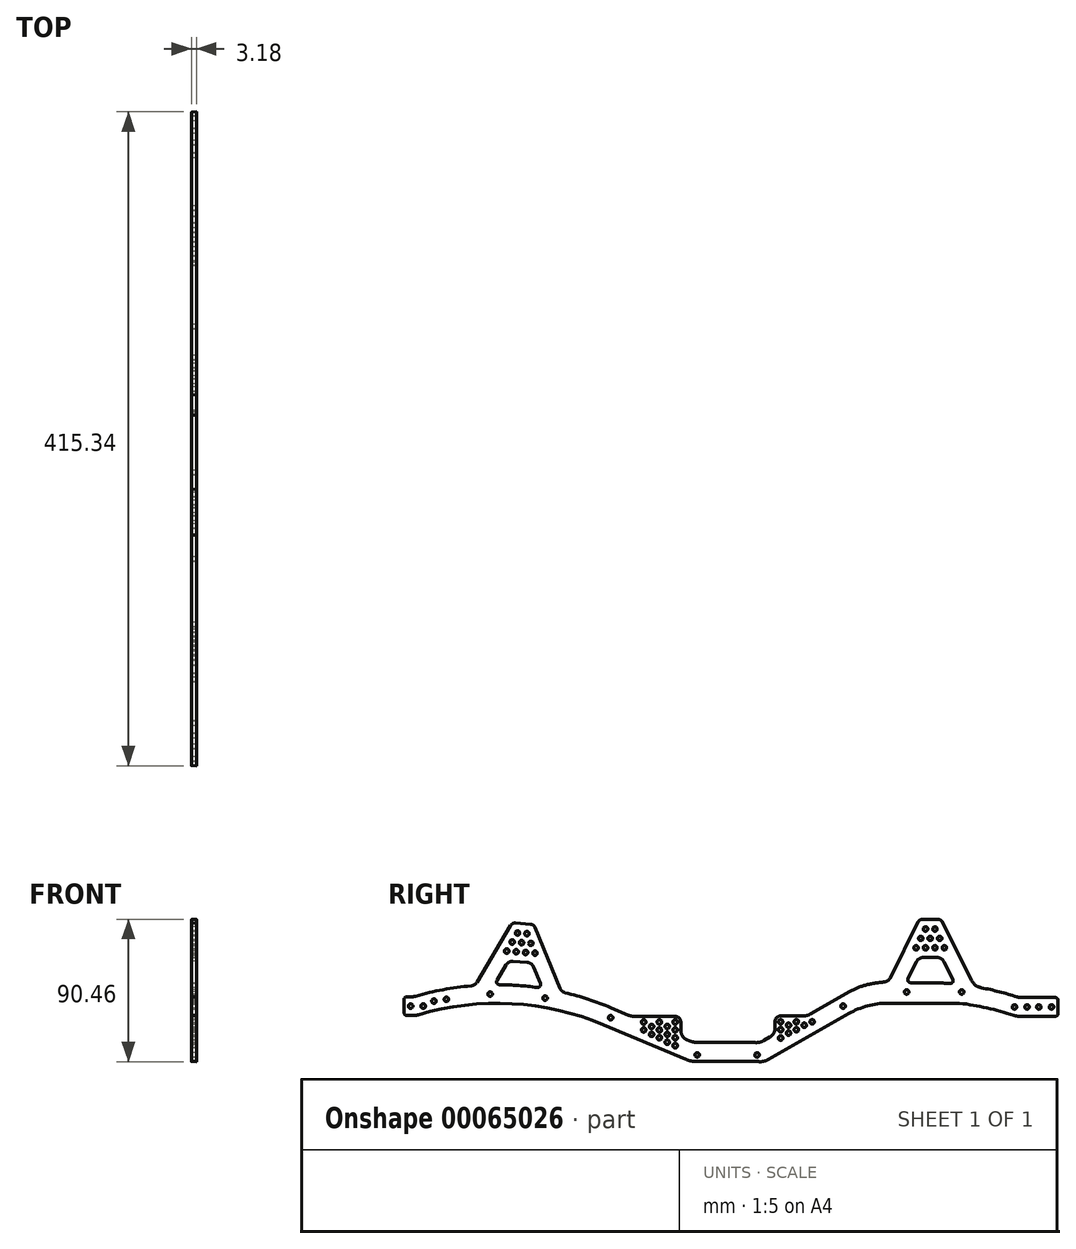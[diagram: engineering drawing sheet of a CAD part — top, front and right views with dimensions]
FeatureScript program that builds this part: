
annotation { "Feature Type Name" : "Feature", "Feature Type Description" : "" }
export const myFeature = defineFeature(function(context is Context, id is Id, definition is map)
    precondition{}
    {
        {
            var Q0;
            Q0=qCreatedBy(makeId("Right.planeOp"),FACE);
            var sketch = newSketch(context, id + "F0", { "sketchPlane" : qUnion([Q0])});
            skLineSegment(sketch, "E0.bottom", {"start": v(-1.5, 0) * mm, "end": v(-24.72, 0) * mm});
            skLineSegment(sketch, "E0.top", {"start": v(-1.5, 11.5) * mm, "end": v(-22.88, 11.5) * mm});
            skLineSegment(sketch, "E0.left", {"start": v(0, 1.5) * mm, "end": v(0, 10) * mm});
            skCircle(sketch, "E1", {"center": v(-4, 5.75) * mm, "radius": 1.59 * mm});
            skPoint(sketch, "E1.centerSnap0", {"position": v(0, 5.75) * mm});
            skCircle(sketch, "E2", {"center": v(-12, 5.75) * mm, "radius": 1.59 * mm});
            skCircle(sketch, "E3", {"center": v(-19.5, 5.75) * mm, "radius": 1.59 * mm});
            skCircle(sketch, "E4", {"center": v(-27.5, 5.75) * mm, "radius": 1.59 * mm});
            skCircle(sketch, "E5", {"center": v(-61, 15.25) * mm, "radius": 1.59 * mm});
            skCircle(sketch, "E6", {"center": v(-96, 15.25) * mm, "radius": 1.59 * mm});
            skLineSegment(sketch, "E7.top", {"start": v(-107.96, 8.28) * mm, "end": v(-62.46, 8.28) * mm});
            skCircle(sketch, "E8", {"center": v(-90, 43.28) * mm, "radius": 1.59 * mm});
            skCircle(sketch, "E9", {"center": v(-84, 43.28) * mm, "radius": 1.59 * mm});
            skCircle(sketch, "E10", {"center": v(-78, 43.28) * mm, "radius": 1.59 * mm});
            skCircle(sketch, "E11", {"center": v(-72, 43.28) * mm, "radius": 1.59 * mm});
            skCircle(sketch, "E12", {"center": v(-87, 49.28) * mm, "radius": 1.59 * mm});
            skCircle(sketch, "E13", {"center": v(-81, 49.28) * mm, "radius": 1.59 * mm});
            skCircle(sketch, "E14", {"center": v(-75, 49.28) * mm, "radius": 1.59 * mm});
            skCircle(sketch, "E15", {"center": v(-84, 55.28) * mm, "radius": 1.59 * mm});
            skCircle(sketch, "E16", {"center": v(-78, 55.28) * mm, "radius": 1.59 * mm});
            skLineSegment(sketch, "E17", {"start": v(-90, 37.39) * mm, "end": v(-90, 67.96) * mm, "construction": true});
            skLineSegment(sketch, "E18", {"start": v(-103.26, 43.28) * mm, "end": v(-65.64, 43.28) * mm, "construction": true});
            skLineSegment(sketch, "E19", {"start": v(-106.28, 24.14) * mm, "end": v(-88.54, 59.62) * mm});
            skLineSegment(sketch, "E20", {"start": v(-85.85, 61.28) * mm, "end": v(-76.15, 61.28) * mm});
            skLineSegment(sketch, "E21", {"start": v(-73.46, 59.62) * mm, "end": v(-54.94, 22.59) * mm});
            skLineSegment(sketch, "E22", {"start": v(-95.22, 23.9) * mm, "end": v(-89.9, 34.52) * mm});
            skLineSegment(sketch, "E23", {"start": v(-85.44, 37.28) * mm, "end": v(-76.56, 37.28) * mm});
            skLineSegment(sketch, "E24", {"start": v(-72.1, 34.52) * mm, "end": v(-66.49, 23.31) * mm});
            skLineSegment(sketch, "E25.trimOffspring", {"start": v(-93.43, 21) * mm, "end": v(-83, 21) * mm});
            skCircle(sketch, "E26", {"center": v(-166, -8.72) * mm, "radius": 1.59 * mm});
            skCircle(sketch, "E27", {"center": v(-166, -3.72) * mm, "radius": 1.59 * mm});
            skCircle(sketch, "E28", {"center": v(-161, -5.86) * mm, "radius": 1.59 * mm});
            skCircle(sketch, "E29", {"center": v(-191, -24.72) * mm, "radius": 1.59 * mm});
            skLineSegment(sketch, "E30", {"start": v(-183.93, -27.53) * mm, "end": v(-132.76, 1.7) * mm});
            skLineSegment(sketch, "E31", {"start": v(-186.53, -15.77) * mm, "end": v(-182.64, -13.55) * mm});
            skLineSegment(sketch, "E32.trimOffspring", {"start": v(-156.92, 1.14) * mm, "end": v(-131.8, 15.49) * mm});
            skLineSegment(sketch, "E33.bottom", {"start": v(-228.31, -17.04) * mm, "end": v(-192.48, -17.04) * mm});
            skCircle(sketch, "E34", {"center": v(-229, -24.72) * mm, "radius": 1.59 * mm});
            skLineSegment(sketch, "E35.trimOffspring", {"start": v(-415.34, -41.7) * mm, "end": v(-30.28, -41.7) * mm, "construction": true});
            skCircle(sketch, "E36", {"center": v(-253, -8.85) * mm, "radius": 1.59 * mm});
            skArc(sketch, "E37", {"start": v(-27.9, 0.52) * mm, "mid": v(-44.98, 5.28) * mm, "end": v(-62.46, 8.28) * mm});
            skArc(sketch, "E38.trimOffspring", {"start": v(-25.96, 11.99) * mm, "mid": v(-37.17, 15.23) * mm, "end": v(-48.57, 17.77) * mm});
            skArc(sketch, "E39.trimOffspring", {"start": v(-68.44, 20.43) * mm, "mid": v(-75.71, 20.86) * mm, "end": v(-83, 21) * mm});
            skArc(sketch, "E40.filletArc", {"start": v(-107.96, 8.28) * mm, "mid": v(-120.79, 6.6) * mm, "end": v(-132.76, 1.7) * mm});
            skPoint(sketch, "E41.visualSharp", {"position": v(-73.47, 37.28) * mm});
            skArc(sketch, "E41.filletArc", {"start": v(-72.1, 34.52) * mm, "mid": v(-73.93, 36.53) * mm, "end": v(-76.56, 37.28) * mm});
            skPoint(sketch, "E42.visualSharp", {"position": v(-88.53, 37.28) * mm});
            skArc(sketch, "E42.filletArc", {"start": v(-85.44, 37.28) * mm, "mid": v(-88.07, 36.53) * mm, "end": v(-89.9, 34.52) * mm});
            skPoint(sketch, "E43.visualSharp", {"position": v(-96.67, 21) * mm});
            skArc(sketch, "E43.filletArc", {"start": v(-95.22, 23.9) * mm, "mid": v(-95.13, 21.95) * mm, "end": v(-93.43, 21) * mm});
            skPoint(sketch, "E44.visualSharp", {"position": v(-64.89, 20.11) * mm});
            skArc(sketch, "E44.filletArc", {"start": v(-68.44, 20.43) * mm, "mid": v(-66.62, 21.3) * mm, "end": v(-66.49, 23.31) * mm});
            skPoint(sketch, "E45.visualSharp", {"position": v(-87.7, 61.28) * mm});
            skArc(sketch, "E45.filletArc", {"start": v(-85.85, 61.28) * mm, "mid": v(-87.43, 60.83) * mm, "end": v(-88.54, 59.62) * mm});
            skPoint(sketch, "E46.visualSharp", {"position": v(-74.3, 61.28) * mm});
            skArc(sketch, "E46.filletArc", {"start": v(-73.46, 59.62) * mm, "mid": v(-74.57, 60.83) * mm, "end": v(-76.15, 61.28) * mm});
            skPoint(sketch, "E47.visualSharp", {"position": v(-52.92, 18.54) * mm});
            skArc(sketch, "E47.filletArc", {"start": v(-54.94, 22.59) * mm, "mid": v(-52.32, 19.43) * mm, "end": v(-48.57, 17.77) * mm});
            skPoint(sketch, "E48.visualSharp", {"position": v(-24.48, 11.5) * mm});
            skArc(sketch, "E48.filletArc", {"start": v(-25.96, 11.99) * mm, "mid": v(-24.44, 11.62) * mm, "end": v(-22.88, 11.5) * mm});
            skPoint(sketch, "E49.visualSharp", {"position": v(-26.38, 0) * mm});
            skArc(sketch, "E49.filletArc", {"start": v(-27.9, 0.52) * mm, "mid": v(-26.33, 0.13) * mm, "end": v(-24.72, 0) * mm});
            skPoint(sketch, "E50.visualSharp", {"position": v(0, 11.5) * mm});
            skArc(sketch, "E50.filletArc", {"start": v(0, 10) * mm, "mid": v(-0.44, 11.06) * mm, "end": v(-1.5, 11.5) * mm});
            skPoint(sketch, "E51.visualSharp", {"position": v(0, 0) * mm});
            skArc(sketch, "E51.filletArc", {"start": v(-1.5, 0) * mm, "mid": v(-0.44, 0.44) * mm, "end": v(0, 1.5) * mm});
            skPoint(sketch, "E52.visualSharp", {"position": v(-169.55, -6.07) * mm});
            skArc(sketch, "E53.filletArc", {"start": v(-192.48, -17.04) * mm, "mid": v(-189.4, -16.87) * mm, "end": v(-186.53, -15.77) * mm});
            skPoint(sketch, "E54.visualSharp", {"position": v(-187.05, -29.31) * mm});
            skArc(sketch, "E54.filletArc", {"start": v(-190.42, -28.72) * mm, "mid": v(-187.07, -28.68) * mm, "end": v(-183.93, -27.53) * mm});
            skLineSegment(sketch, "E55", {"start": v(-107.44, 25.98) * mm, "end": v(-107.44, 25.98) * mm});
            skLineSegment(sketch, "E56", {"start": v(-190.42, -28.72) * mm, "end": v(-230.42, -28.65) * mm});
            skCircle(sketch, "E57", {"center": v(-253, -13.85) * mm, "radius": 1.59 * mm});
            skCircle(sketch, "E58", {"center": v(-253, -3.85) * mm, "radius": 1.59 * mm});
            skCircle(sketch, "E59", {"center": v(-258, -6.68) * mm, "radius": 1.59 * mm});
            skCircle(sketch, "E60", {"center": v(-411, 6.28) * mm, "radius": 1.59 * mm});
            skLineSegment(sketch, "E61", {"start": v(-411, 6.28) * mm, "end": v(-205.2, 8.89) * mm, "construction": true});
            skCircle(sketch, "E62", {"center": v(-403, 6.28) * mm, "radius": 1.59 * mm});
            skLineSegment(sketch, "E63", {"start": v(-415, 2.03) * mm, "end": v(-415, 10.53) * mm});
            skCircle(sketch, "E64", {"center": v(-360.5, 13.92) * mm, "radius": 1.59 * mm});
            skCircle(sketch, "E65", {"center": v(-325.6, 11.36) * mm, "radius": 1.59 * mm});
            skCircle(sketch, "E66", {"center": v(-396.21, 9.47) * mm, "radius": 1.59 * mm});
            skCircle(sketch, "E67", {"center": v(-388.29, 10.57) * mm, "radius": 1.59 * mm});
            skCircle(sketch, "E68", {"center": v(-284, -1.11) * mm, "radius": 1.59 * mm});
            skArc(sketch, "E69", {"start": v(-288.38, -5.48) * mm, "mid": v(-346.64, 7.96) * mm, "end": v(-406.02, 0.95) * mm});
            skArc(sketch, "E70", {"start": v(-283.9, 5.12) * mm, "mid": v(-298.2, 10.46) * mm, "end": v(-312.88, 14.62) * mm});
            skLineSegment(sketch, "E71", {"start": v(-413.5, 12.03) * mm, "end": v(-410.53, 12.03) * mm});
            skLineSegment(sketch, "E72", {"start": v(-413.5, 0.53) * mm, "end": v(-408.88, 0.53) * mm});
            skLineSegment(sketch, "E73", {"start": v(-236.22, -27.47) * mm, "end": v(-288.38, -5.48) * mm});
            skLineSegment(sketch, "E74", {"start": v(-234.14, -15.86) * mm, "end": v(-235.68, -15.21) * mm});
            skPoint(sketch, "E75.visualSharp", {"position": v(-169.43, -0.18) * mm});
            skPoint(sketch, "E76.visualSharp", {"position": v(-159.22, -0.18) * mm});
            skArc(sketch, "E76.filletArc", {"start": v(-161.88, -0.18) * mm, "mid": v(-159.31, 0.16) * mm, "end": v(-156.92, 1.14) * mm});
            skLineSegment(sketch, "E77", {"start": v(-360.5, 13.92) * mm, "end": v(-325.6, 11.36) * mm, "construction": true});
            skLineSegment(sketch, "E78", {"start": v(-322.64, 51.7) * mm, "end": v(-325.6, 11.36) * mm, "construction": true});
            skLineSegment(sketch, "E79", {"start": v(-357.62, 53.24) * mm, "end": v(-360.5, 13.92) * mm, "construction": true});
            skCircle(sketch, "E80", {"center": v(-340.56, 46.55) * mm, "radius": 1.59 * mm});
            skLineSegment(sketch, "E81", {"start": v(-358.02, 47.83) * mm, "end": v(-323.1, 45.27) * mm, "construction": true});
            skCircle(sketch, "E82", {"center": v(-334.58, 46.11) * mm, "radius": 1.59 * mm});
            skCircle(sketch, "E83", {"center": v(-346.55, 46.99) * mm, "radius": 1.59 * mm});
            skCircle(sketch, "E84", {"center": v(-349.98, 41.22) * mm, "radius": 1.59 * mm});
            skCircle(sketch, "E85", {"center": v(-344, 40.79) * mm, "radius": 1.59 * mm});
            skCircle(sketch, "E86", {"center": v(-338, 40.35) * mm, "radius": 1.59 * mm});
            skCircle(sketch, "E87", {"center": v(-332.02, 39.9) * mm, "radius": 1.59 * mm});
            skCircle(sketch, "E88", {"center": v(-343.12, 52.75) * mm, "radius": 1.59 * mm});
            skCircle(sketch, "E89", {"center": v(-337.13, 52.31) * mm, "radius": 1.59 * mm});
            skLineSegment(sketch, "E90", {"start": v(-357.58, 53.81) * mm, "end": v(-322.67, 51.25) * mm, "construction": true});
            skLineSegment(sketch, "E91", {"start": v(-358.45, 41.84) * mm, "end": v(-323.55, 39.29) * mm, "construction": true});
            skLineSegment(sketch, "E92", {"start": v(-339.67, 58.73) * mm, "end": v(-341.5, 33.86) * mm, "construction": true});
            skLineSegment(sketch, "E93", {"start": v(-347.32, 57.41) * mm, "end": v(-368.74, 21.42) * mm});
            skLineSegment(sketch, "E94", {"start": v(-344.53, 58.87) * mm, "end": v(-334.84, 58.16) * mm});
            skLineSegment(sketch, "E95", {"start": v(-332.29, 56.31) * mm, "end": v(-316.34, 17.58) * mm});
            skLineSegment(sketch, "E96", {"start": v(-356.32, 22.74) * mm, "end": v(-350.53, 32.48) * mm});
            skLineSegment(sketch, "E97", {"start": v(-345.86, 34.9) * mm, "end": v(-337.01, 34.26) * mm});
            skLineSegment(sketch, "E98", {"start": v(-332.75, 31.17) * mm, "end": v(-328.44, 20.7) * mm});
            skCircle(sketch, "E99", {"center": v(-263, -3.85) * mm, "radius": 1.59 * mm});
            skCircle(sketch, "E100", {"center": v(-263, -8.85) * mm, "radius": 1.59 * mm});
            skEllipticalArc(sketch, "E101.trimOffspring", {});
            skPoint(sketch, "E102.visualSharp", {"position": v(-127.63, 17.87) * mm});
            skArc(sketch, "E102.filletArc", {"start": v(-120.81, 19.76) * mm, "mid": v(-126.46, 18.03) * mm, "end": v(-131.8, 15.49) * mm});
            skPoint(sketch, "E103.visualSharp", {"position": v(-107.55, 21.59) * mm});
            skArc(sketch, "E103.filletArc", {"start": v(-110.32, 21.4) * mm, "mid": v(-107.94, 22.24) * mm, "end": v(-106.28, 24.14) * mm});
            skCircle(sketch, "E104", {"center": v(-136.33, 6.28) * mm, "radius": 1.59 * mm});
            skPoint(sketch, "E105.visualSharp", {"position": v(-233.44, -28.64) * mm});
            skArc(sketch, "E105.filletArc", {"start": v(-236.22, -27.47) * mm, "mid": v(-233.38, -28.35) * mm, "end": v(-230.42, -28.65) * mm});
            skPoint(sketch, "E106.visualSharp", {"position": v(-231.34, -17.04) * mm});
            skArc(sketch, "E106.filletArc", {"start": v(-234.14, -15.86) * mm, "mid": v(-231.28, -16.74) * mm, "end": v(-228.31, -17.04) * mm});
            skPoint(sketch, "E107.visualSharp", {"position": v(-249.54, -0.18) * mm});
            skPoint(sketch, "E108.newPointB", {"position": v(-284, 5.15) * mm});
            skLineSegment(sketch, "E109", {"start": v(-284, 5.15) * mm, "end": v(-272.64, 0.37) * mm});
            skPoint(sketch, "E110.visualSharp", {"position": v(-270.72, -0.44) * mm});
            skArc(sketch, "E110.filletArc", {"start": v(-272.64, 0.37) * mm, "mid": v(-270.68, -0.23) * mm, "end": v(-268.63, -0.42) * mm});
            skPoint(sketch, "E111.visualSharp", {"position": v(-348.95, 35.13) * mm});
            skArc(sketch, "E111.filletArc", {"start": v(-345.86, 34.9) * mm, "mid": v(-348.54, 34.35) * mm, "end": v(-350.53, 32.48) * mm});
            skPoint(sketch, "E112.visualSharp", {"position": v(-333.93, 34.03) * mm});
            skArc(sketch, "E112.filletArc", {"start": v(-332.75, 31.17) * mm, "mid": v(-334.45, 33.32) * mm, "end": v(-337.01, 34.26) * mm});
            skArc(sketch, "E113.trimOffspring", {"start": v(-330.57, 17.95) * mm, "mid": v(-342.56, 19.22) * mm, "end": v(-354.62, 19.72) * mm});
            skArc(sketch, "E114.trimOffspring", {"start": v(-372.6, 19) * mm, "mid": v(-390.34, 16.55) * mm, "end": v(-407.76, 12.42) * mm});
            skPoint(sketch, "E115.visualSharp", {"position": v(-358.12, 19.71) * mm});
            skArc(sketch, "E115.filletArc", {"start": v(-356.32, 22.74) * mm, "mid": v(-356.35, 20.73) * mm, "end": v(-354.62, 19.72) * mm});
            skPoint(sketch, "E116.visualSharp", {"position": v(-327.1, 17.44) * mm});
            skArc(sketch, "E116.filletArc", {"start": v(-330.57, 17.95) * mm, "mid": v(-328.7, 18.7) * mm, "end": v(-328.44, 20.7) * mm});
            skPoint(sketch, "E117.visualSharp", {"position": v(-370.06, 19.2) * mm});
            skArc(sketch, "E117.filletArc", {"start": v(-372.6, 19) * mm, "mid": v(-370.38, 19.74) * mm, "end": v(-368.74, 21.42) * mm});
            skPoint(sketch, "E118.visualSharp", {"position": v(-315.36, 15.2) * mm});
            skArc(sketch, "E118.filletArc", {"start": v(-316.34, 17.58) * mm, "mid": v(-314.97, 15.68) * mm, "end": v(-312.88, 14.62) * mm});
            skPoint(sketch, "E119.visualSharp", {"position": v(-333, 58.03) * mm});
            skArc(sketch, "E119.filletArc", {"start": v(-332.29, 56.31) * mm, "mid": v(-333.3, 57.6) * mm, "end": v(-334.84, 58.16) * mm});
            skPoint(sketch, "E120.visualSharp", {"position": v(-346.38, 59) * mm});
            skArc(sketch, "E120.filletArc", {"start": v(-344.53, 58.87) * mm, "mid": v(-346.13, 58.54) * mm, "end": v(-347.32, 57.41) * mm});
            skPoint(sketch, "E121.visualSharp", {"position": v(-415, 12.03) * mm});
            skArc(sketch, "E121.filletArc", {"start": v(-413.5, 12.03) * mm, "mid": v(-414.56, 11.6) * mm, "end": v(-415, 10.53) * mm});
            skPoint(sketch, "E122.visualSharp", {"position": v(-415, 0.53) * mm});
            skArc(sketch, "E122.filletArc", {"start": v(-415, 2.03) * mm, "mid": v(-414.56, 0.97) * mm, "end": v(-413.5, 0.53) * mm});
            skPoint(sketch, "E123.visualSharp", {"position": v(-409.1, 12.03) * mm});
            skArc(sketch, "E123.filletArc", {"start": v(-410.53, 12.03) * mm, "mid": v(-409.13, 12.13) * mm, "end": v(-407.76, 12.42) * mm});
            skPoint(sketch, "E124.visualSharp", {"position": v(-407.4, 0.53) * mm});
            skArc(sketch, "E124.filletArc", {"start": v(-408.88, 0.53) * mm, "mid": v(-407.43, 0.63) * mm, "end": v(-406.02, 0.95) * mm});
            skPoint(sketch, "E125.visualSharp", {"position": v(-244.23, -0.42) * mm});
            skPoint(sketch, "E126.visualSharp", {"position": v(-244.23, -11.61) * mm});
            skPoint(sketch, "E52.filletArc.end.orphan", {"position": v(-169.53, -5.18) * mm});
            skPoint(sketch, "E127.center.orphan", {"position": v(-258, -11.68) * mm});
            skCircle(sketch, "E128", {"center": v(-258, -11.68) * mm, "radius": 1.59 * mm});
            skPoint(sketch, "E129.center.orphan", {"position": v(-248, -13.85) * mm});
            skPoint(sketch, "E130.center.orphan", {"position": v(-248, -8.85) * mm});
            skPoint(sketch, "E125.filletArc.center.orphan", {"position": v(-248, -3.85) * mm});
            skCircle(sketch, "E131", {"center": v(-248, -16.68) * mm, "radius": 1.59 * mm});
            skCircle(sketch, "E132", {"center": v(-248, -11.68) * mm, "radius": 1.59 * mm});
            skCircle(sketch, "E133", {"center": v(-248, -6.68) * mm, "radius": 1.59 * mm});
            skCircle(sketch, "E134", {"center": v(-243, -8.85) * mm, "radius": 1.59 * mm});
            skCircle(sketch, "E135", {"center": v(-243, -3.85) * mm, "radius": 1.59 * mm});
            skCircle(sketch, "E136", {"center": v(-243, -13.85) * mm, "radius": 1.59 * mm});
            skCircle(sketch, "E137", {"center": v(-243, -18.85) * mm, "radius": 1.59 * mm});
            skLineSegment(sketch, "E138", {"start": v(-268.63, -0.42) * mm, "end": v(-243, -0.42) * mm});
            skLineSegment(sketch, "E139", {"start": v(-239.56, -3.85) * mm, "end": v(-239.56, -9.36) * mm});
            skPoint(sketch, "E140.visualSharp", {"position": v(-239.56, -13.58) * mm});
            skArc(sketch, "E140.filletArc", {"start": v(-239.56, -9.36) * mm, "mid": v(-238.5, -12.87) * mm, "end": v(-235.68, -15.21) * mm});
            skPoint(sketch, "E141.visualSharp", {"position": v(-239.56, -0.42) * mm});
            skArc(sketch, "E141.filletArc", {"start": v(-239.56, -3.85) * mm, "mid": v(-240.57, -1.42) * mm, "end": v(-243, -0.42) * mm});
            skPoint(sketch, "E142.center.orphan", {"position": v(-156, -3.72) * mm});
            skPoint(sketch, "E143.center.orphan", {"position": v(-156, -8.7) * mm});
            skCircle(sketch, "E144", {"center": v(-156, -3.72) * mm, "radius": 1.59 * mm});
            skCircle(sketch, "E145", {"center": v(-171, -10.86) * mm, "radius": 1.59 * mm});
            skCircle(sketch, "E146", {"center": v(-171, -5.86) * mm, "radius": 1.59 * mm});
            skCircle(sketch, "E147", {"center": v(-176, -3.72) * mm, "radius": 1.59 * mm});
            skCircle(sketch, "E148", {"center": v(-176, -8.7) * mm, "radius": 1.59 * mm});
            skCircle(sketch, "E149", {"center": v(-176, -14.02) * mm, "radius": 1.59 * mm});
            skLineSegment(sketch, "E150", {"start": v(-179.44, -8.04) * mm, "end": v(-179.44, -3.6) * mm});
            skLineSegment(sketch, "E151", {"start": v(-161.88, -0.18) * mm, "end": v(-176, -0.18) * mm});
            skPoint(sketch, "E152.visualSharp", {"position": v(-179.44, -11.72) * mm});
            skArc(sketch, "E152.filletArc", {"start": v(-182.64, -13.55) * mm, "mid": v(-180.3, -11.22) * mm, "end": v(-179.44, -8.04) * mm});
            skPoint(sketch, "E153.visualSharp", {"position": v(-179.44, -0.18) * mm});
            skArc(sketch, "E153.filletArc", {"start": v(-176, -0.18) * mm, "mid": v(-178.43, -1.18) * mm, "end": v(-179.44, -3.6) * mm});
            skPoint(sketch, "E154.center.orphan", {"position": v(-176, -19.02) * mm});
            skPoint(sketch, "E155.center.orphan", {"position": v(-171, -15.87) * mm});
            skPoint(sketch, "E156.center.orphan", {"position": v(-166, -13.72) * mm});
            skPoint(sketch, "E157.center.orphan", {"position": v(-161, -10.86) * mm});
            skPoint(sketch, "E158.center.orphan", {"position": v(-156, -8.72) * mm});
            const initialGuessF0  = {"E101.trimOffspring": [-0.11163260042667389, 0.0004979297518730164, -0.9901239733853069, -0.1401945695370975, 0.04015003435592223, 0.02062460912675176, 4.606780417992475, 4.872183828327888]};
            skSetInitialGuess(sketch, initialGuessF0);
            skSolve(sketch);
        }
        {
            var Q0;
            Q0 = qSketchRegion(id + "F0", true);
            extrude(context, id + "F1", {"entities" : qUnion([Q0]), "depth" : 3.17 * mm, "hasDraft" : true, "draftAngle" : 3 * degree});
        }
    });
